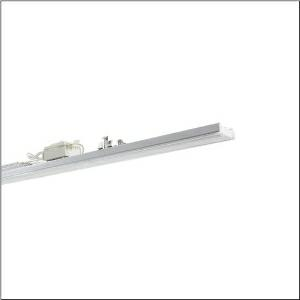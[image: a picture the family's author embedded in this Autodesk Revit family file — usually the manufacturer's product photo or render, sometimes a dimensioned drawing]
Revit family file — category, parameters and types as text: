
# Revit family: licross_r__11_recessed_ho_51te11mn4exs_738b
name_source: partatom
category: Lighting Fixtures
units: mm (PartAtom-declared; Revit-internal decimal feet)

## family parameters
Cut with Voids When Loaded = No
Host = Face
Light Source = No
Part Type = Normal
Room Calculation Point = No
Round Connector Dimension = Use Diameter
Shared = No

## types (1)
- --- (1 x LED, 14070 lm, 74.5 W, 4000K)
    Apparent Load = 75 VA
    CIE Flux Codes = 87 95 99 100 100
    Color Rendering = 80
    Color Temperature = 4000K
    Default Elevation = 1800 mm
    Description = Licross® 11 Recessed HO, luminaire insert, of sheet steel, galvanised, coil coated, white, length: 1.500mm, width: 66mm, height: 67mm, LED rated luminous flux: 14.070lm, light colour: 840, control gear: ON/OFF Multilumen, with plug, 3-pole, with phase selection, mains connection: 220..240V, AC, 50/60Hz, rated input power: 75W, halogen-free wiring, primary light control with lens, of plastic, primary optical cover: cover, of PMMA, light emission: direct distribution, primary light characteristic: symmetric, protection rating (complete): IP54, insulation class (complete): insulation class I (protective earthing), certification: CE, ENEC, VDE, UKCA, protection symbol: D if used in an environment with non-conductive dust loads with corresponding accessories, impact resistance: IK06, permissible ambient temperature for indoor applications: -35..+35°C, corresponds to IFS (International Featured Standards) requirements for safety and quality in the food industry, reducing of maximum allowable ambient temperature of 5°C with ceiling mounting, packaging unit: 1 piece
    Height = 58 mm
    Lamp = 1 x LED
    Lamp Light Flux = 14070 lm
    Lamp Power = 74.5 W
    Lamp count = 1
    Length = 1500 mm
    Luminous efficacy = 189 lm/W
    Manufacturer = Siteco
    ModVariant = No
    Model = 51TE11MN4EXS
    Mounting Place = Ceiling
    Mounting Type = Pendant
    Number of Poles = 1
    OnlyDefault = Yes
    Power Factor = 1
    Product Name = Licross® 11 Recessed HO
    Product group = luminaire insert
    ProductGroupID = 902
    Protection Class = Protection class I
    Protection Degree = IP 54
    RLX_Detail_Level = 1
    RLX_Emergency_Light_Flux = 0 lm
    RLX_Emergency_Type = 0
    RLX_Emergency_Type_DB = No
    RlxData = <blob elided: 22149 chars, md5=71354789>
    Socket = socket
    Standby Power = 0 W
    System Light Flux = 14070 lm
    System Power = 75 W
    Type Comments = factory setting: luminous flux: 100 % | (A | C | E) | 174 mA
    Type Image = l_1296930.jpg
    URL = http://relux.com
    VarID = @adj_084566
    Voltage = 0 V
    Weight = 0.00 kg
    Width = 66 mm

## geometry (parser evidence)
native form markers: Blend x4, Sweep x9
no freeform markers — native parametric forms only
